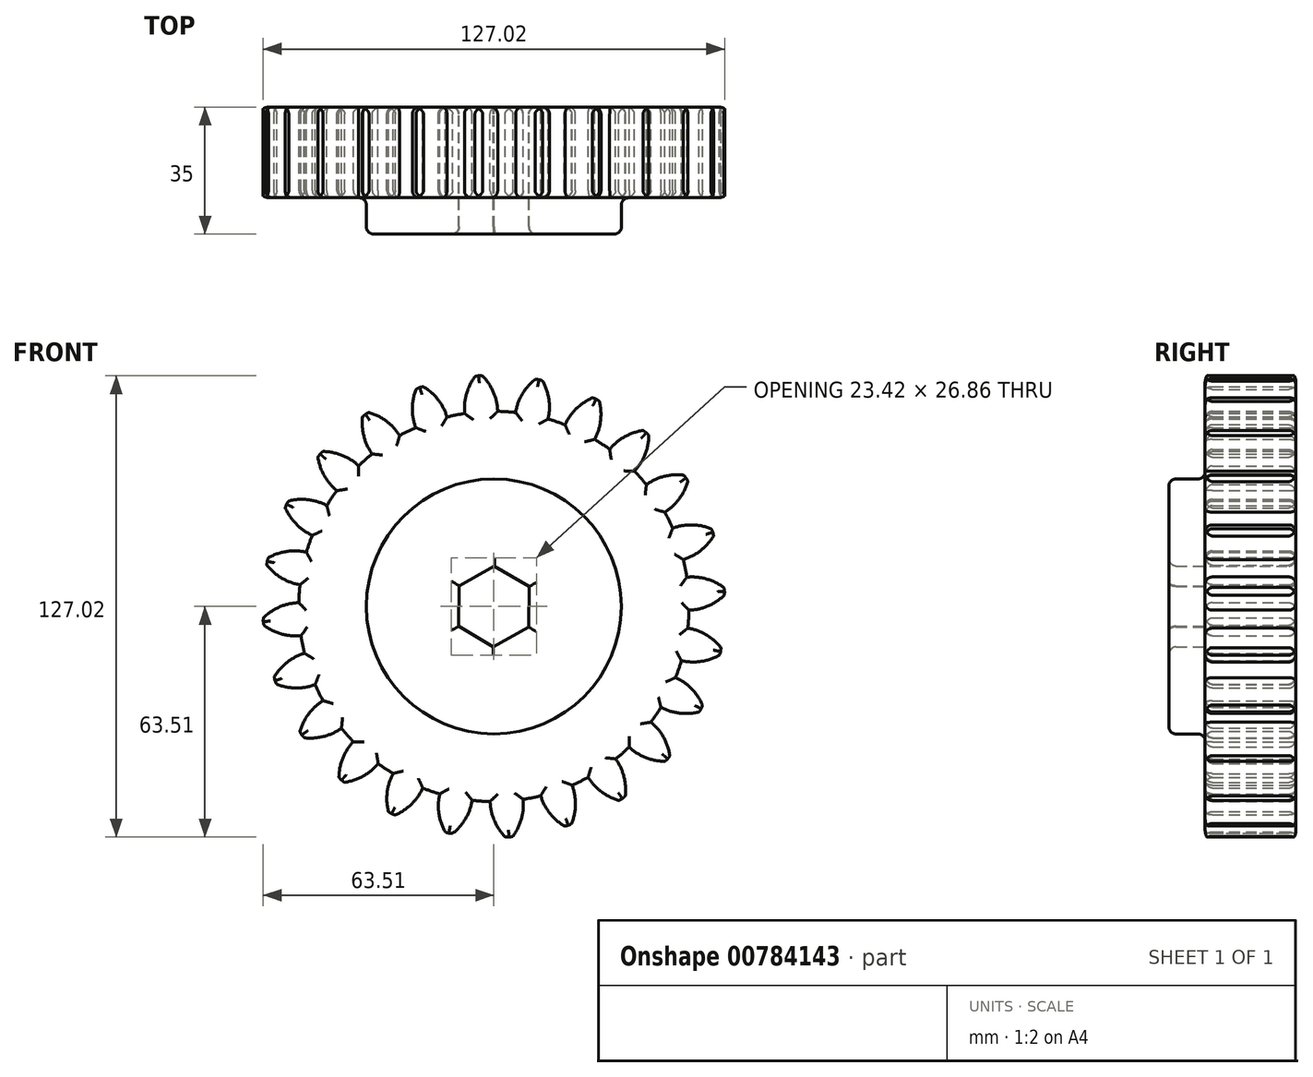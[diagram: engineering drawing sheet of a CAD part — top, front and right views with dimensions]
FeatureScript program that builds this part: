
annotation { "Feature Type Name" : "Feature", "Feature Type Description" : "" }
export const myFeature = defineFeature(function(context is Context, id is Id, definition is map)
    precondition{}
    {
        {
            var Q0;
            Q0=qCreatedBy(makeId("Front.planeOp"),FACE);
            var sketch = newSketch(context, id + "F0", { "sketchPlane" : qUnion([Q0])});
            skCircle(sketch, "E0", {"center": v(0, 0) * mm, "radius": 53.72 * mm});
            skCircle(sketch, "E1", {"center": v(0, 0) * mm, "radius": 58.67 * mm, "construction": true});
            skCircle(sketch, "E2", {"center": v(0, 0) * mm, "radius": 63.5 * mm, "construction": true});
            skLineSegment(sketch, "E3", {"start": v(0, 0) * mm, "end": v(0, 118.64) * mm});
            skLineSegment(sketch, "E4", {"start": v(0, 0) * mm, "end": v(-8.6, 131.21) * mm, "construction": true});
            skLineSegment(sketch, "E5", {"start": v(0, 58.67) * mm, "end": v(-49.7, 57.15) * mm, "construction": true});
            skLineSegment(sketch, "E6", {"start": v(0, 58.67) * mm, "end": v(-55.04, 36.71) * mm, "construction": true});
            skCircle(sketch, "E7", {"center": v(0, 0) * mm, "radius": 54.5 * mm, "construction": true});
            skCircle(sketch, "E8", {"center": v(0, 58.67) * mm, "radius": 14.6 * mm, "construction": true});
            skCircle(sketch, "E9", {"center": v(-13.57, 53.26) * mm, "radius": 14.6 * mm, "construction": true});
            skArc(sketch, "E10", {"start": v(0, 58.67) * mm, "mid": v(-1.31, 61.2) * mm, "end": v(-3.08, 63.43) * mm});
            skArc(sketch, "E11", {"start": v(1.03, 53.71) * mm, "mid": v(0.74, 56.24) * mm, "end": v(0, 58.67) * mm});
            skArc(sketch, "E12.MirrorCS", {"start": v(-7.66, 58.17) * mm, "mid": v(-6.68, 60.84) * mm, "end": v(-5.23, 63.28) * mm});
            skArc(sketch, "E13.MirrorCS", {"start": v(-8.03, 53.12) * mm, "mid": v(-8.08, 55.66) * mm, "end": v(-7.66, 58.17) * mm});
            skArc(sketch, "E14", {"start": v(-3.08, 63.43) * mm, "mid": v(-4.16, 63.5) * mm, "end": v(-5.23, 63.28) * mm});
            skCircle(sketch, "E15", {"center": v(0, 0) * mm, "radius": 35.1 * mm});
            skCircle(sketch, "E16.cCircle", {"center": v(0, 0) * mm, "radius": 9.63 * mm, "construction": true});
            skLineSegment(sketch, "E16.0", {"start": v(9.57, -5.67) * mm, "end": v(-0.13, -11.12) * mm});
            skLineSegment(sketch, "E16.1", {"start": v(-0.13, -11.12) * mm, "end": v(-9.7, -5.45) * mm});
            skLineSegment(sketch, "E16.2", {"start": v(-9.7, -5.45) * mm, "end": v(-9.57, 5.67) * mm});
            skLineSegment(sketch, "E16.3", {"start": v(-9.57, 5.67) * mm, "end": v(0.13, 11.12) * mm});
            skLineSegment(sketch, "E16.4", {"start": v(0.13, 11.12) * mm, "end": v(9.7, 5.45) * mm});
            skLineSegment(sketch, "E16.5", {"start": v(9.7, 5.45) * mm, "end": v(9.57, -5.67) * mm});
            skPoint(sketch, "E16.0.midPoint", {"position": v(4.72, -8.4) * mm});
            skSolve(sketch);
        }
        {
            var Q0;
            Q0=qSketchRegion(id+"F0",true);
            extrude(context, id + "F1", {"entities" : qUnion([Q0]), "depth" : 25 * mm, "offsetDistance" : 25 * mm});
        }
        {
            var Q0;
            Q0=makeQuery(id+"F1.opExtrude","SWEPT_BODY",BODY,{"disambiguationData":[OSD([sQuery(id+"F0.wireOp",EDGE,"E0"),sQuery(id+"F0.wireOp",EDGE,"E10"),sQuery(id+"F0.wireOp",EDGE,"E11"),sQuery(id+"F0.wireOp",EDGE,"E12.MirrorCS"),sQuery(id+"F0.wireOp",EDGE,"E13.MirrorCS"),sQuery(id+"F0.wireOp",EDGE,"E14")])]});
            var Q1;
            Q1=makeQuery(id+"F1.opExtrude","SWEPT_FACE",FACE,{"disambiguationData":[OSD([sQuery(id+"F0.wireOp",EDGE,"E0")])]});
            circularPattern(context, id + "F2", {"entities" : qUnion([Q0]), "axis" : qUnion([Q1]), "angle" : 360 * degree, "instanceCount" : 24, "equalSpace" : true});
        }
        {
            var Q0;
            Q0=makeQuery(id+"F0.imprint","IMPRINT",FACE,{"disambiguationData":[TD([[makeQuery(id+"F0.imprint","IMPRINT",EDGE,{"derivedFrom":sQuery(id+"F0.wireOp",EDGE,"E15")}),1.0]])]});
            extrude(context, id + "F3", {"entities" : qUnion([Q0]), "operationType" : NewBodyOperationType.ADD, "depth" : 35 * mm, "offsetDistance" : 25 * mm});
        }
        {
            var Q0;
            Q0=makeQuery(id+"F3.opExtrude","CAP_FACE",FACE,{"disambiguationData":[OSD([sQuery(id+"F0.wireOp",EDGE,"E15"),sQuery(id+"F0.wireOp",EDGE,"E16.0"),sQuery(id+"F0.wireOp",EDGE,"E16.1"),sQuery(id+"F0.wireOp",EDGE,"E16.2"),sQuery(id+"F0.wireOp",EDGE,"E16.3"),sQuery(id+"F0.wireOp",EDGE,"E16.4"),sQuery(id+"F0.wireOp",EDGE,"E16.5")])],"isStart":false});
            var Q1;
            {var subQ0=sQuery(id+"F0.wireOp",EDGE,"E15");var subQ1=makeQuery(id+"F1.opExtrude","CAP_FACE",FACE,{"disambiguationData":[OSD([sQuery(id+"F0.wireOp",EDGE,"E0"),sQuery(id+"F0.wireOp",EDGE,"E10"),sQuery(id+"F0.wireOp",EDGE,"E11"),sQuery(id+"F0.wireOp",EDGE,"E12.MirrorCS"),sQuery(id+"F0.wireOp",EDGE,"E13.MirrorCS"),sQuery(id+"F0.wireOp",EDGE,"E14"),subQ0])],"isStart":true});Q1=makeQuery(id+"F3.boolean.opBoolean","MERGE",FACE,{"derivedFrom":[subQ1,makeQuery(id+"F2.opPattern","COPY",FACE,{"derivedFrom":subQ1,"instanceName":"1"}),makeQuery(id+"F2.opPattern","COPY",FACE,{"derivedFrom":subQ1,"instanceName":"2"}),makeQuery(id+"F2.opPattern","COPY",FACE,{"derivedFrom":subQ1,"instanceName":"3"}),makeQuery(id+"F2.opPattern","COPY",FACE,{"derivedFrom":subQ1,"instanceName":"4"}),makeQuery(id+"F2.opPattern","COPY",FACE,{"derivedFrom":subQ1,"instanceName":"5"}),makeQuery(id+"F2.opPattern","COPY",FACE,{"derivedFrom":subQ1,"instanceName":"6"}),makeQuery(id+"F2.opPattern","COPY",FACE,{"derivedFrom":subQ1,"instanceName":"7"}),makeQuery(id+"F2.opPattern","COPY",FACE,{"derivedFrom":subQ1,"instanceName":"8"}),makeQuery(id+"F2.opPattern","COPY",FACE,{"derivedFrom":subQ1,"instanceName":"9"}),makeQuery(id+"F2.opPattern","COPY",FACE,{"derivedFrom":subQ1,"instanceName":"10"}),makeQuery(id+"F2.opPattern","COPY",FACE,{"derivedFrom":subQ1,"instanceName":"11"}),makeQuery(id+"F2.opPattern","COPY",FACE,{"derivedFrom":subQ1,"instanceName":"12"}),makeQuery(id+"F2.opPattern","COPY",FACE,{"derivedFrom":subQ1,"instanceName":"13"}),makeQuery(id+"F2.opPattern","COPY",FACE,{"derivedFrom":subQ1,"instanceName":"14"}),makeQuery(id+"F2.opPattern","COPY",FACE,{"derivedFrom":subQ1,"instanceName":"15"}),makeQuery(id+"F2.opPattern","COPY",FACE,{"derivedFrom":subQ1,"instanceName":"16"}),makeQuery(id+"F2.opPattern","COPY",FACE,{"derivedFrom":subQ1,"instanceName":"17"}),makeQuery(id+"F2.opPattern","COPY",FACE,{"derivedFrom":subQ1,"instanceName":"18"}),makeQuery(id+"F2.opPattern","COPY",FACE,{"derivedFrom":subQ1,"instanceName":"19"}),makeQuery(id+"F2.opPattern","COPY",FACE,{"derivedFrom":subQ1,"instanceName":"20"}),makeQuery(id+"F2.opPattern","COPY",FACE,{"derivedFrom":subQ1,"instanceName":"21"}),makeQuery(id+"F2.opPattern","COPY",FACE,{"derivedFrom":subQ1,"instanceName":"22"}),makeQuery(id+"F2.opPattern","COPY",FACE,{"derivedFrom":subQ1,"instanceName":"23"}),makeQuery(id+"F3.opExtrude","CAP_FACE",FACE,{"disambiguationData":[OSD([subQ0,sQuery(id+"F0.wireOp",EDGE,"E16.0"),sQuery(id+"F0.wireOp",EDGE,"E16.1"),sQuery(id+"F0.wireOp",EDGE,"E16.2"),sQuery(id+"F0.wireOp",EDGE,"E16.3"),sQuery(id+"F0.wireOp",EDGE,"E16.4"),sQuery(id+"F0.wireOp",EDGE,"E16.5")])],"isStart":true})]});}
            var Q2;
            {var subQ0=makeQuery(id+"F1.opExtrude","CAP_FACE",FACE,{"disambiguationData":[OSD([sQuery(id+"F0.wireOp",EDGE,"E0"),sQuery(id+"F0.wireOp",EDGE,"E10"),sQuery(id+"F0.wireOp",EDGE,"E11"),sQuery(id+"F0.wireOp",EDGE,"E12.MirrorCS"),sQuery(id+"F0.wireOp",EDGE,"E13.MirrorCS"),sQuery(id+"F0.wireOp",EDGE,"E14"),sQuery(id+"F0.wireOp",EDGE,"E15")])],"isStart":false});Q2=makeQuery(id+"F3.boolean.opBoolean","MERGE",FACE,{"derivedFrom":[subQ0,makeQuery(id+"F2.opPattern","COPY",FACE,{"derivedFrom":subQ0,"instanceName":"1"}),makeQuery(id+"F2.opPattern","COPY",FACE,{"derivedFrom":subQ0,"instanceName":"2"}),makeQuery(id+"F2.opPattern","COPY",FACE,{"derivedFrom":subQ0,"instanceName":"3"}),makeQuery(id+"F2.opPattern","COPY",FACE,{"derivedFrom":subQ0,"instanceName":"4"}),makeQuery(id+"F2.opPattern","COPY",FACE,{"derivedFrom":subQ0,"instanceName":"5"}),makeQuery(id+"F2.opPattern","COPY",FACE,{"derivedFrom":subQ0,"instanceName":"6"}),makeQuery(id+"F2.opPattern","COPY",FACE,{"derivedFrom":subQ0,"instanceName":"7"}),makeQuery(id+"F2.opPattern","COPY",FACE,{"derivedFrom":subQ0,"instanceName":"8"}),makeQuery(id+"F2.opPattern","COPY",FACE,{"derivedFrom":subQ0,"instanceName":"9"}),makeQuery(id+"F2.opPattern","COPY",FACE,{"derivedFrom":subQ0,"instanceName":"10"}),makeQuery(id+"F2.opPattern","COPY",FACE,{"derivedFrom":subQ0,"instanceName":"11"}),makeQuery(id+"F2.opPattern","COPY",FACE,{"derivedFrom":subQ0,"instanceName":"12"}),makeQuery(id+"F2.opPattern","COPY",FACE,{"derivedFrom":subQ0,"instanceName":"13"}),makeQuery(id+"F2.opPattern","COPY",FACE,{"derivedFrom":subQ0,"instanceName":"14"}),makeQuery(id+"F2.opPattern","COPY",FACE,{"derivedFrom":subQ0,"instanceName":"15"}),makeQuery(id+"F2.opPattern","COPY",FACE,{"derivedFrom":subQ0,"instanceName":"16"}),makeQuery(id+"F2.opPattern","COPY",FACE,{"derivedFrom":subQ0,"instanceName":"17"}),makeQuery(id+"F2.opPattern","COPY",FACE,{"derivedFrom":subQ0,"instanceName":"18"}),makeQuery(id+"F2.opPattern","COPY",FACE,{"derivedFrom":subQ0,"instanceName":"19"}),makeQuery(id+"F2.opPattern","COPY",FACE,{"derivedFrom":subQ0,"instanceName":"20"}),makeQuery(id+"F2.opPattern","COPY",FACE,{"derivedFrom":subQ0,"instanceName":"21"}),makeQuery(id+"F2.opPattern","COPY",FACE,{"derivedFrom":subQ0,"instanceName":"22"}),makeQuery(id+"F2.opPattern","COPY",FACE,{"derivedFrom":subQ0,"instanceName":"23"})]});}
            fillet(context, id + "F4", {"entities" : qUnion([Q0, Q1, Q2]), "radius" : 2 * mm, "tangentPropagation" : true, "allowEdgeOverflow" : false});
        }
    });
